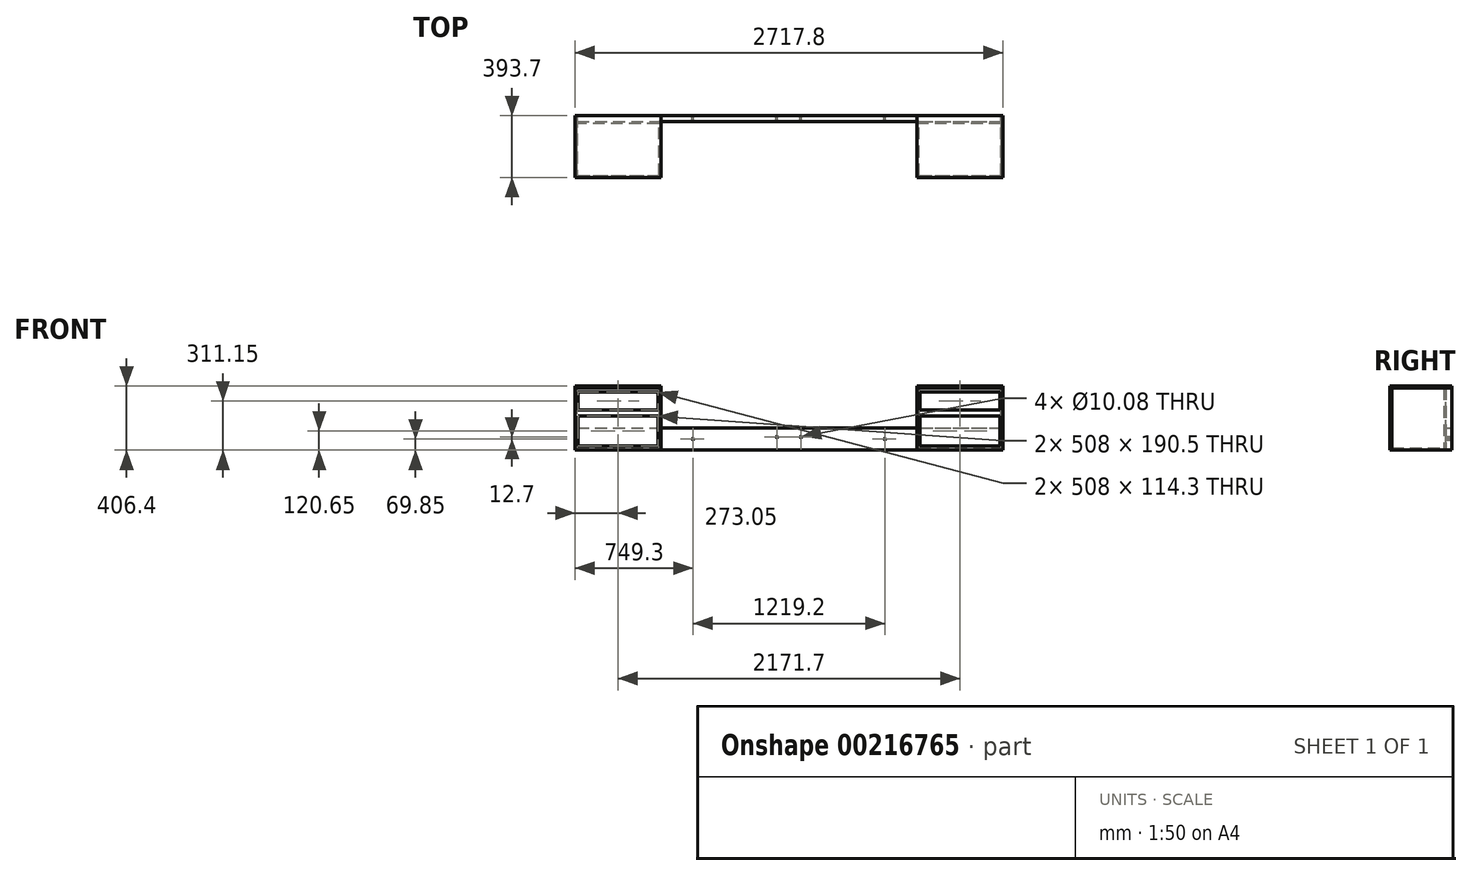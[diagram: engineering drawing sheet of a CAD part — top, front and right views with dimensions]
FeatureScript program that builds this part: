
annotation { "Feature Type Name" : "Feature", "Feature Type Description" : "" }
export const myFeature = defineFeature(function(context is Context, id is Id, definition is map)
    precondition{}
    {
        {
            var Q0;
            Q0=qCreatedBy(makeId("Front.planeOp"),FACE);
            var sketch = newSketch(context, id + "F0", { "sketchPlane" : qUnion([Q0])});
            skLineSegment(sketch, "E0.bottom", {"start": v(0, 0) * mm, "end": v(2692.4, 0) * mm});
            skLineSegment(sketch, "E0.top", {"start": v(0, 139.7) * mm, "end": v(2692.4, 139.7) * mm});
            skLineSegment(sketch, "E0.left", {"start": v(0, 0) * mm, "end": v(0, 139.7) * mm});
            skLineSegment(sketch, "E0.right", {"start": v(2692.4, 0) * mm, "end": v(2692.4, 139.7) * mm});
            skSolve(sketch);
        }
        {
            var Q0;
            Q0=makeQuery(id+"F0.imprint","IMPRINT",FACE,{"disambiguationData":[TD([[makeQuery(id+"F0.imprint","IMPRINT",EDGE,{"derivedFrom":sQuery(id+"F0.wireOp",EDGE,"E0.bottom")}),1.0]])]});
            extrude(context, id + "F1", {"entities" : qUnion([Q0]), "depth" : 38.1 * mm});
        }
        {
            var Q0;
            Q0=makeQuery(id+"F1.opExtrude","CAP_FACE",FACE,{"disambiguationData":[OSD([sQuery(id+"F0.wireOp",EDGE,"E0.bottom"),sQuery(id+"F0.wireOp",EDGE,"E0.top"),sQuery(id+"F0.wireOp",EDGE,"E0.left"),sQuery(id+"F0.wireOp",EDGE,"E0.right")])],"isStart":false});
            var sketch = newSketch(context, id + "F2", { "sketchPlane" : qUnion([Q0])});
            skLineSegment(sketch, "E1", {"start": v(533.4, 139.7) * mm, "end": v(533.4, 0) * mm});
            skLineSegment(sketch, "E2", {"start": v(2159, 0) * mm, "end": v(2159, 139.7) * mm});
            skSolve(sketch);
        }
        {
            var Q0;
            Q0=makeQuery(id+"F1.opExtrude","SWEPT_FACE",FACE,{"disambiguationData":[OSD([sQuery(id+"F0.wireOp",EDGE,"E0.left")])]});
            var sketch = newSketch(context, id + "F3", { "sketchPlane" : qUnion([Q0])});
            skLineSegment(sketch, "E3.bottom", {"start": v(0, 0) * mm, "end": v(381, 0) * mm});
            skLineSegment(sketch, "E3.top", {"start": v(0, 393.7) * mm, "end": v(381, 393.7) * mm});
            skLineSegment(sketch, "E3.left", {"start": v(0, 0) * mm, "end": v(0, 393.7) * mm});
            skLineSegment(sketch, "E3.right", {"start": v(381, 0) * mm, "end": v(381, 393.7) * mm});
            skSolve(sketch);
        }
        {
            var Q0;
            {var subQ4=sQuery(id+"F3.wireOp",EDGE,"E3.top");Q0=makeQuery(id+"F3.imprint","IMPRINT",FACE,{"disambiguationData":[TD([[makeQuery(id+"F3.imprint","IMPRINT",EDGE,{"derivedFrom":subQ4}),-1.0]])]});}
            var Q1;
            {var subQ3=sQuery(id+"F0.wireOp",EDGE,"E0.left");var subQ4=makeQuery(id+"F1.opExtrude","CAP_EDGE",EDGE,{"disambiguationData":[OSD([subQ3])],"isStart":false});Q1=makeQuery(id+"F3.imprint","IMPRINT",FACE,{"disambiguationData":[TD([[makeQuery(id+"F3.imprint","IMPRINT",EDGE,{"derivedFrom":subQ4}),1.0]])]});}
            extrude(context, id + "F4", {"entities" : qUnion([Q0, Q1]), "depth" : 12.7 * mm});
        }
        {
            var Q0;
            Q0=makeQuery(id+"F4.opExtrude","SWEPT_BODY",BODY,{"disambiguationData":[OSD([sQuery(id+"F3.wireOp",EDGE,"E3.bottom"),sQuery(id+"F3.wireOp",EDGE,"E3.top"),sQuery(id+"F3.wireOp",EDGE,"E3.left"),sQuery(id+"F3.wireOp",EDGE,"E3.right")])]});
            transform(context, id + "F5", {"entities" : qUnion([Q0]), "transformType" : TransformType.TRANSLATION_3D, "dx" : 2705.1 * mm, "dy" : 0 * mm, "dz" : 0 * mm, "makeCopy" : true});
        }
        {
            var Q0;
            {var subQ0=sQuery(id+"F2.wireOp",EDGE,"E1");Q0=makeQuery(id+"F2.imprint","IMPRINT",FACE,{"disambiguationData":[TD([[makeQuery(id+"F2.imprint","IMPRINT",EDGE,{"derivedFrom":subQ0}),-1.0]])]});}
            var sketch = newSketch(context, id + "F6", { "sketchPlane" : qUnion([Q0])});
            skLineSegment(sketch, "E4.0", {"start": v(533.4, 139.7) * mm, "end": v(533.4, 0) * mm});
            skLineSegment(sketch, "E5.bottom", {"start": v(533.4, 0) * mm, "end": v(520.7, 0) * mm});
            skLineSegment(sketch, "E5.top", {"start": v(533.4, 393.7) * mm, "end": v(520.7, 393.7) * mm});
            skLineSegment(sketch, "E5.left", {"start": v(533.4, 0) * mm, "end": v(533.4, 393.7) * mm});
            skLineSegment(sketch, "E5.right", {"start": v(520.7, 0) * mm, "end": v(520.7, 393.7) * mm});
            skSolve(sketch);
        }
        {
            var Q0;
            {var subQ0=sQuery(id+"F6.wireOp",EDGE,"E5.top");Q0=makeQuery(id+"F6.imprint","IMPRINT",FACE,{"disambiguationData":[TD([[makeQuery(id+"F6.imprint","IMPRINT",EDGE,{"derivedFrom":subQ0}),1.0]])]});}
            var Q1;
            {var subQ0=sQuery(id+"F6.wireOp",EDGE,"E5.bottom");Q1=makeQuery(id+"F6.imprint","IMPRINT",FACE,{"disambiguationData":[TD([[makeQuery(id+"F6.imprint","IMPRINT",EDGE,{"derivedFrom":subQ0}),1.0]])]});}
            var Q2;
            Q2=makeQuery(id+"F4.opExtrude","SWEPT_FACE",FACE,{"disambiguationData":[OSD([sQuery(id+"F3.wireOp",EDGE,"E3.right")])]});
            extrude(context, id + "F7", {"entities" : qUnion([Q0, Q1]), "endBound" : BoundingType.UP_TO_SURFACE, "endBoundEntityFace" : qUnion([Q2]), "depth" : 25.4 * mm});
        }
        {
            var Q0;
            Q0=makeQuery(id+"F7.opExtrude","SWEPT_BODY",BODY,{"disambiguationData":[OSD([sQuery(id+"F6.wireOp",EDGE,"E5.bottom"),sQuery(id+"F6.wireOp",EDGE,"E5.top"),sQuery(id+"F6.wireOp",EDGE,"E5.left"),sQuery(id+"F6.wireOp",EDGE,"E5.right")])]});
            transform(context, id + "F8", {"entities" : qUnion([Q0]), "transformType" : TransformType.TRANSLATION_3D, "dx" : 1638.3 * mm, "dy" : 0 * mm, "dz" : 0 * mm, "makeCopy" : true});
        }
        {
            var Q0;
            Q0=makeQuery(id+"F4.opExtrude","CAP_FACE",FACE,{"disambiguationData":[OSD([sQuery(id+"F3.wireOp",EDGE,"E3.bottom"),sQuery(id+"F3.wireOp",EDGE,"E3.top"),sQuery(id+"F3.wireOp",EDGE,"E3.left"),sQuery(id+"F3.wireOp",EDGE,"E3.right")])],"isStart":true});
            var sketch = newSketch(context, id + "F9", { "sketchPlane" : qUnion([Q0])});
            skLineSegment(sketch, "E6.0", {"start": v(-38.1, 0) * mm, "end": v(-38.1, 139.7) * mm});
            skLineSegment(sketch, "E7.top", {"start": v(-38.1, 393.7) * mm, "end": v(-50.8, 393.7) * mm});
            skLineSegment(sketch, "E7.left", {"start": v(-38.1, 12.7) * mm, "end": v(-38.1, 393.7) * mm});
            skLineSegment(sketch, "E7.right", {"start": v(-50.8, 12.7) * mm, "end": v(-50.8, 393.7) * mm});
            skLineSegment(sketch, "E8", {"start": v(-50.8, 12.7) * mm, "end": v(-38.1, 12.7) * mm});
            skSolve(sketch);
        }
        {
            var Q0;
            {var subQ3=sQuery(id+"F9.wireOp",EDGE,"E7.top");Q0=makeQuery(id+"F9.imprint","IMPRINT",FACE,{"disambiguationData":[TD([[makeQuery(id+"F9.imprint","IMPRINT",EDGE,{"derivedFrom":subQ3}),1.0]])]});}
            extrude(context, id + "F10", {"entities" : qUnion([Q0]), "endBound" : BoundingType.UP_TO_NEXT, "depth" : 25.4 * mm});
        }
        {
            var Q0;
            Q0=makeQuery(id+"F10.opExtrude","SWEPT_BODY",BODY,{"disambiguationData":[OSD([sQuery(id+"F9.wireOp",EDGE,"E7.top"),sQuery(id+"F9.wireOp",EDGE,"E7.left"),sQuery(id+"F9.wireOp",EDGE,"E7.right"),sQuery(id+"F9.wireOp",EDGE,"E8")])]});
            transform(context, id + "F11", {"entities" : qUnion([Q0]), "transformType" : TransformType.TRANSLATION_3D, "dx" : 2171.7 * mm, "dy" : 0 * mm, "dz" : 0 * mm, "makeCopy" : true});
        }
        {
            var Q0;
            {var subQ0=sQuery(id+"F2.wireOp",EDGE,"E1");Q0=makeQuery(id+"F2.imprint","IMPRINT",FACE,{"disambiguationData":[TD([[makeQuery(id+"F2.imprint","IMPRINT",EDGE,{"derivedFrom":subQ0}),-1.0]])]});}
            var sketch = newSketch(context, id + "F12", { "sketchPlane" : qUnion([Q0])});
            skLineSegment(sketch, "E9.0", {"start": v(520.7, 12.7) * mm, "end": v(0, 12.7) * mm});
            skLineSegment(sketch, "E10.0", {"start": v(0, 0) * mm, "end": v(0, 139.7) * mm});
            skLineSegment(sketch, "E11.0", {"start": v(520.7, 0) * mm, "end": v(520.7, 393.7) * mm});
            skLineSegment(sketch, "E12.bottom", {"start": v(520.7, 0) * mm, "end": v(0, 0) * mm});
            skLineSegment(sketch, "E12.left", {"start": v(520.7, 0) * mm, "end": v(520.7, 12.7) * mm});
            skLineSegment(sketch, "E12.right", {"start": v(0, 0) * mm, "end": v(0, 12.7) * mm});
            skSolve(sketch);
        }
        {
            var Q0;
            Q0 = qSketchRegion(id + "F12", true);
            var Q1;
            Q1=makeQuery(id+"F4.opExtrude","SWEPT_FACE",FACE,{"disambiguationData":[OSD([sQuery(id+"F3.wireOp",EDGE,"E3.right")])]});
            extrude(context, id + "F13", {"entities" : qUnion([Q0]), "endBound" : BoundingType.UP_TO_SURFACE, "endBoundEntityFace" : qUnion([Q1]), "depth" : 25.4 * mm});
        }
        {
            var Q0;
            Q0=makeQuery(id+"F13.opExtrude","SWEPT_BODY",BODY,{"disambiguationData":[OSD([sQuery(id+"F12.wireOp",EDGE,"E12.bottom"),sQuery(id+"F12.wireOp",EDGE,"E9.0"),sQuery(id+"F12.wireOp",EDGE,"E12.left"),sQuery(id+"F12.wireOp",EDGE,"E12.right")])]});
            transform(context, id + "F14", {"entities" : qUnion([Q0]), "transformType" : TransformType.TRANSLATION_3D, "dx" : 2171.7 * mm, "dy" : 0 * mm, "dz" : 0 * mm, "makeCopy" : true});
        }
        {
            var Q0;
            Q0=makeQuery(id+"F8.opPattern","COPY",FACE,{"derivedFrom":makeQuery(id+"F7.opExtrude","CAP_FACE",FACE,{"disambiguationData":[OSD([sQuery(id+"F6.wireOp",EDGE,"E5.bottom"),sQuery(id+"F6.wireOp",EDGE,"E5.top"),sQuery(id+"F6.wireOp",EDGE,"E5.left"),sQuery(id+"F6.wireOp",EDGE,"E5.right")])],"isStart":false}),"instanceName":"1"});
            var sketch = newSketch(context, id + "F15", { "sketchPlane" : qUnion([Q0])});
            skLineSegment(sketch, "E13.0", {"start": v(2705.1, 0) * mm, "end": v(2705.1, 393.7) * mm});
            skLineSegment(sketch, "E14.bottom", {"start": v(2159, 0) * mm, "end": v(2705.1, 0) * mm});
            skLineSegment(sketch, "E14.top", {"start": v(2159, 393.7) * mm, "end": v(2705.1, 393.7) * mm});
            skLineSegment(sketch, "E14.left", {"start": v(2159, 0) * mm, "end": v(2159, 393.7) * mm});
            skLineSegment(sketch, "E15.bottom", {"start": v(2178.05, 368.3) * mm, "end": v(2686.05, 368.3) * mm});
            skLineSegment(sketch, "E15.top", {"start": v(2178.05, 254) * mm, "end": v(2686.05, 254) * mm});
            skLineSegment(sketch, "E15.left", {"start": v(2178.05, 368.3) * mm, "end": v(2178.05, 254) * mm});
            skLineSegment(sketch, "E15.right", {"start": v(2686.05, 368.3) * mm, "end": v(2686.05, 254) * mm});
            skLineSegment(sketch, "E16.bottom", {"start": v(2178.05, 215.9) * mm, "end": v(2686.05, 215.9) * mm});
            skLineSegment(sketch, "E16.top", {"start": v(2178.05, 25.4) * mm, "end": v(2686.05, 25.4) * mm});
            skLineSegment(sketch, "E16.left", {"start": v(2178.05, 215.9) * mm, "end": v(2178.05, 25.4) * mm});
            skLineSegment(sketch, "E16.right", {"start": v(2686.05, 215.9) * mm, "end": v(2686.05, 25.4) * mm});
            skSolve(sketch);
        }
        {
            var Q0;
            {var subQ5=sQuery(id+"F15.wireOp",EDGE,"E13.0");Q0=makeQuery(id+"F15.imprint","IMPRINT",FACE,{"disambiguationData":[TD([[makeQuery(id+"F15.imprint","IMPRINT",EDGE,{"derivedFrom":subQ5}),1.0]])]});}
            var Q1;
            {var subQ5=sQuery(id+"F15.wireOp",EDGE,"E14.left");Q1=makeQuery(id+"F15.imprint","IMPRINT",FACE,{"disambiguationData":[TD([[makeQuery(id+"F15.imprint","IMPRINT",EDGE,{"derivedFrom":subQ5}),1.0]])]});}
            extrude(context, id + "F16", {"entities" : qUnion([Q0, Q1]), "depth" : 12.7 * mm});
        }
        {
            var Q0;
            Q0=makeQuery(id+"F16.opExtrude","SWEPT_BODY",BODY,{"disambiguationData":[OSD([sQuery(id+"F15.wireOp",EDGE,"E14.bottom"),sQuery(id+"F15.wireOp",EDGE,"E14.top"),sQuery(id+"F15.wireOp",EDGE,"E14.left"),sQuery(id+"F15.wireOp",EDGE,"E13.0"),sQuery(id+"F15.wireOp",EDGE,"E15.bottom"),sQuery(id+"F15.wireOp",EDGE,"E15.top"),sQuery(id+"F15.wireOp",EDGE,"E15.left"),sQuery(id+"F15.wireOp",EDGE,"E15.right"),sQuery(id+"F15.wireOp",EDGE,"E16.bottom"),sQuery(id+"F15.wireOp",EDGE,"E16.top"),sQuery(id+"F15.wireOp",EDGE,"E16.left"),sQuery(id+"F15.wireOp",EDGE,"E16.right")])]});
            transform(context, id + "F17", {"entities" : qUnion([Q0]), "transformType" : TransformType.TRANSLATION_3D, "dx" : -2171.7 * mm, "dy" : 0 * mm, "dz" : 0 * mm, "makeCopy" : true});
        }
        {
            var Q0;
            Q0=makeQuery(id+"F4.opExtrude","SWEPT_FACE",FACE,{"disambiguationData":[OSD([sQuery(id+"F3.wireOp",EDGE,"E3.top")])]});
            var sketch = newSketch(context, id + "F18", { "sketchPlane" : qUnion([Q0])});
            skLineSegment(sketch, "E17.0", {"start": v(-12.7, -393.7) * mm, "end": v(533.4, -393.7) * mm});
            skLineSegment(sketch, "E18.bottom", {"start": v(-12.7, 0) * mm, "end": v(533.4, 0) * mm});
            skLineSegment(sketch, "E18.left", {"start": v(-12.7, 0) * mm, "end": v(-12.7, -393.7) * mm});
            skLineSegment(sketch, "E18.right", {"start": v(533.4, 0) * mm, "end": v(533.4, -393.7) * mm});
            skSolve(sketch);
        }
        {
            var Q0;
            {var subQ3=sQuery(id+"F18.wireOp",EDGE,"E17.0");Q0=makeQuery(id+"F18.imprint","IMPRINT",FACE,{"disambiguationData":[TD([[makeQuery(id+"F18.imprint","IMPRINT",EDGE,{"derivedFrom":subQ3}),1.0]])]});}
            var Q1;
            {var subQ1=sQuery(id+"F3.wireOp",EDGE,"E3.top");var subQ2=makeQuery(id+"F4.opExtrude","CAP_EDGE",EDGE,{"disambiguationData":[OSD([subQ1])],"isStart":true});Q1=makeQuery(id+"F18.imprint","IMPRINT",FACE,{"disambiguationData":[TD([[makeQuery(id+"F18.imprint","IMPRINT",EDGE,{"derivedFrom":subQ2}),-1.0]])]});}
            extrude(context, id + "F19", {"entities" : qUnion([Q0, Q1]), "depth" : 12.7 * mm});
        }
        {
            var Q0;
            Q0=makeQuery(id+"F19.opExtrude","SWEPT_BODY",BODY,{"disambiguationData":[OSD([sQuery(id+"F18.wireOp",EDGE,"E18.bottom"),sQuery(id+"F18.wireOp",EDGE,"E17.0"),sQuery(id+"F18.wireOp",EDGE,"E18.left"),sQuery(id+"F18.wireOp",EDGE,"E18.right")])]});
            transform(context, id + "F20", {"entities" : qUnion([Q0]), "transformType" : TransformType.TRANSLATION_3D, "dx" : 2171.7 * mm, "dy" : 0 * mm, "dz" : 0 * mm, "makeCopy" : true});
        }
        {
            var Q0;
            Q0=makeQuery(id+"F1.opExtrude","CAP_FACE",FACE,{"disambiguationData":[OSD([sQuery(id+"F0.wireOp",EDGE,"E0.bottom"),sQuery(id+"F0.wireOp",EDGE,"E0.top"),sQuery(id+"F0.wireOp",EDGE,"E0.left"),sQuery(id+"F0.wireOp",EDGE,"E0.right")])],"isStart":true});
            var sketch = newSketch(context, id + "F21", { "sketchPlane" : qUnion([Q0])});
            skPoint(sketch, "E19", {"position": v(-1955.8, 69.85) * mm});
            skPoint(sketch, "E20", {"position": v(-736.6, 69.85) * mm});
            skPoint(sketch, "E21", {"position": v(-1270, 82.55) * mm});
            skPoint(sketch, "E22", {"position": v(-1422.4, 82.55) * mm});
            skSolve(sketch);
        }
        {
            var Q0;
            Q0=sQuery(id+"F21.wireOp",VERTEX,"E19");
            var Q1;
            Q1=sQuery(id+"F21.wireOp",VERTEX,"E22");
            var Q2;
            Q2=sQuery(id+"F21.wireOp",VERTEX,"E21");
            var Q3;
            Q3=sQuery(id+"F21.wireOp",VERTEX,"E20");
            var Q4;
            Q4=makeQuery(id+"F1.opExtrude","SWEPT_BODY",BODY,{"disambiguationData":[OSD([sQuery(id+"F0.wireOp",EDGE,"E0.bottom"),sQuery(id+"F0.wireOp",EDGE,"E0.top"),sQuery(id+"F0.wireOp",EDGE,"E0.left"),sQuery(id+"F0.wireOp",EDGE,"E0.right")])]});
            hole(context, id + "F22", {"style" : HoleStyle.SIMPLE, "endStyle" : HoleEndStyle.BLIND, "standardTappedOrClearance" : lookupTablePath({ "standard" : "ANSI", "fit" : "Normal (ASME)", "size" : "3/8", "type" : "Clearance" }), "standardBlindInLast" : lookupTablePath({ "fit" : "Free", "standard" : "ANSI", "size" : "3/8", "type" : "Clearance" }), "holeDiameter" : 10.08 * mm, "holeDepth" : 50.8 * mm, "startFromSketch" : true, "locations" : qUnion([Q0, Q1, Q2, Q3]), "scope" : qUnion([Q4])});
        }
    });
